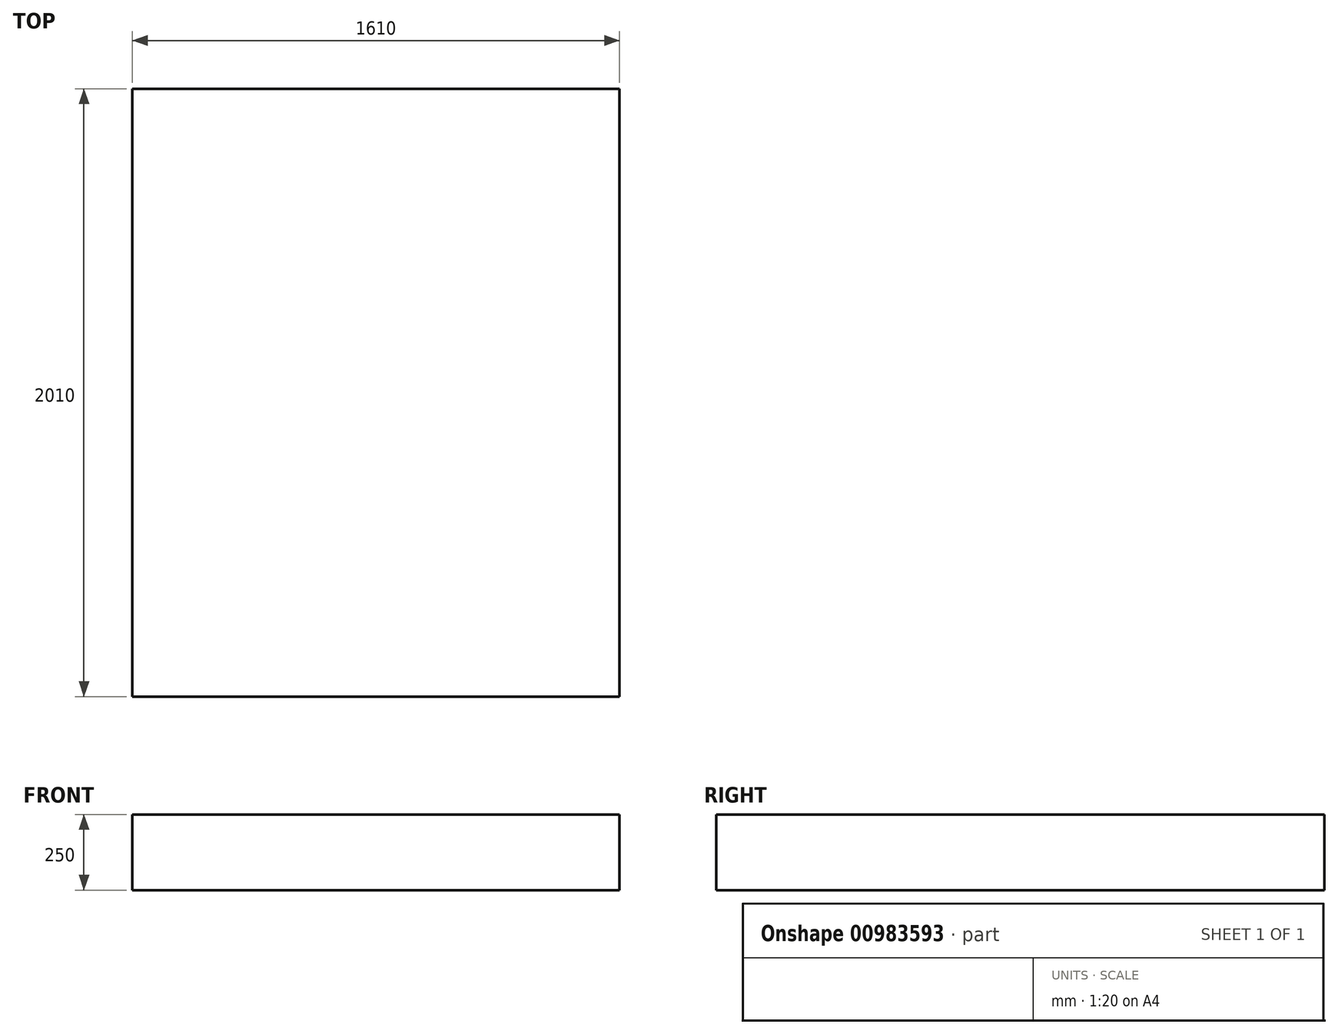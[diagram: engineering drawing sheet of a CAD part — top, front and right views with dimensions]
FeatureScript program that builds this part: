
annotation { "Feature Type Name" : "Feature", "Feature Type Description" : "" }
export const myFeature = defineFeature(function(context is Context, id is Id, definition is map)
    precondition{}
    {
        {
            var Q0;
            Q0=qCreatedBy(makeId("Top.planeOp"),FACE);
            var sketch = newSketch(context, id + "F0", { "sketchPlane" : qUnion([Q0])});
            skLineSegment(sketch, "E0.bottom", {"start": v(-805, 1005) * mm, "end": v(805, 1005) * mm});
            skLineSegment(sketch, "E0.top", {"start": v(-805, -1005) * mm, "end": v(805, -1005) * mm});
            skLineSegment(sketch, "E0.left", {"start": v(-805, 1005) * mm, "end": v(-805, -1005) * mm});
            skLineSegment(sketch, "E0.right", {"start": v(805, 1005) * mm, "end": v(805, -1005) * mm});
            skPoint(sketch, "E0.middle", {"position": v(0, 0) * mm});
            skSolve(sketch);
        }
        {
            var Q0;
            Q0=makeQuery(id+"F0.imprint","IMPRINT",FACE,{"disambiguationData":[TD([[makeQuery(id+"F0.imprint","IMPRINT",EDGE,{"derivedFrom":sQuery(id+"F0.wireOp",EDGE,"E0.bottom")}),-1.0]])]});
            extrude(context, id + "F1", {"entities" : qUnion([Q0]), "depth" : 250 * mm, "offsetDistance" : 25 * mm});
        }
    });
